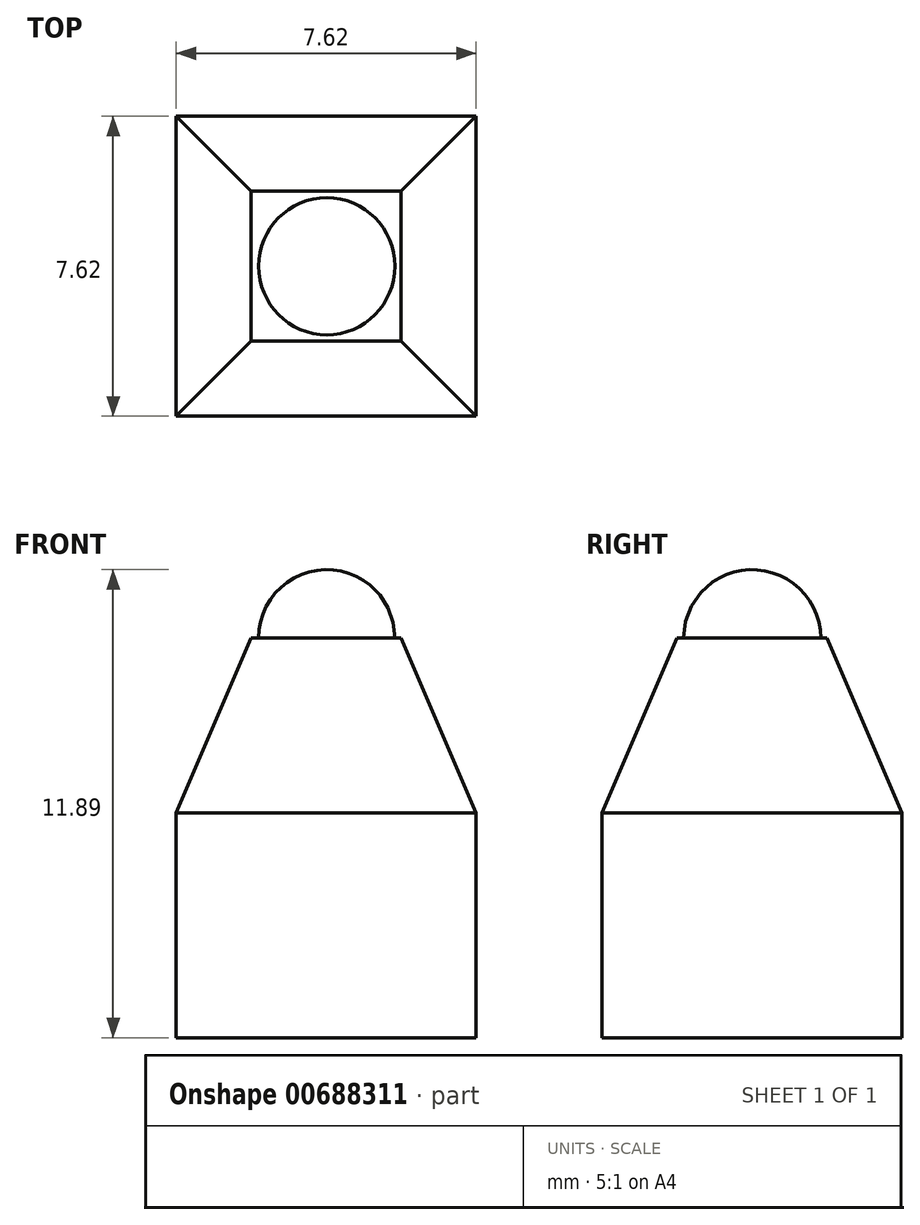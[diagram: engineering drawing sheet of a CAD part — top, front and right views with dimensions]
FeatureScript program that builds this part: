
annotation { "Feature Type Name" : "Feature", "Feature Type Description" : "" }
export const myFeature = defineFeature(function(context is Context, id is Id, definition is map)
    precondition{}
    {
        {
            var Q0;
            Q0=qCreatedBy(makeId("Top.planeOp"),FACE);
            var sketch = newSketch(context, id + "F0", { "sketchPlane" : qUnion([Q0])});
            skLineSegment(sketch, "E0.bottom", {"start": v(0, 0) * mm, "end": v(7.62, 0) * mm});
            skLineSegment(sketch, "E0.top", {"start": v(0, 7.62) * mm, "end": v(7.62, 7.62) * mm});
            skLineSegment(sketch, "E0.left", {"start": v(0, 0) * mm, "end": v(0, 7.62) * mm});
            skLineSegment(sketch, "E0.right", {"start": v(7.62, 0) * mm, "end": v(7.62, 7.62) * mm});
            skSolve(sketch);
        }
        {
            var Q0;
            Q0=makeQuery(id+"F0.imprint","IMPRINT",FACE,{"disambiguationData":[TD([[makeQuery(id+"F0.imprint","IMPRINT",EDGE,{"derivedFrom":sQuery(id+"F0.wireOp",EDGE,"E0.bottom")}),1.0]])]});
            extrude(context, id + "F1", {"entities" : qUnion([Q0]), "depth" : 10.16 * mm, "offsetDistance" : 25.4 * mm});
        }
        {
            var Q0;
            Q0=makeQuery(id+"F1.opExtrude","CAP_EDGE",EDGE,{"disambiguationData":[OSD([sQuery(id+"F0.wireOp",EDGE,"E0.left")])],"isStart":false});
            var Q1;
            Q1=makeQuery(id+"F1.opExtrude","CAP_EDGE",EDGE,{"disambiguationData":[OSD([sQuery(id+"F0.wireOp",EDGE,"E0.right")])],"isStart":false});
            chamfer(context, id + "F2", {"entities" : qUnion([Q0, Q1]), "chamferType" : ChamferType.TWO_OFFSETS, "width1" : 4.44 * mm, "oppositeDirection" : false, "width2" : 1.9 * mm, "tangentPropagation" : true});
        }
        {
            var Q0;
            Q0=makeQuery(id+"F1.opExtrude","CAP_EDGE",EDGE,{"disambiguationData":[OSD([sQuery(id+"F0.wireOp",EDGE,"E0.bottom")])],"isStart":false});
            var Q1;
            Q1=makeQuery(id+"F1.opExtrude","CAP_EDGE",EDGE,{"disambiguationData":[OSD([sQuery(id+"F0.wireOp",EDGE,"E0.top")])],"isStart":false});
            chamfer(context, id + "F3", {"entities" : qUnion([Q0, Q1]), "chamferType" : ChamferType.TWO_OFFSETS, "width1" : 1.9 * mm, "oppositeDirection" : false, "width2" : 4.44 * mm, "tangentPropagation" : true});
        }
        {
            var Q0;
            Q0=makeQuery(id+"F1.opExtrude","CAP_FACE",FACE,{"disambiguationData":[OSD([sQuery(id+"F0.wireOp",EDGE,"E0.bottom"),sQuery(id+"F0.wireOp",EDGE,"E0.top"),sQuery(id+"F0.wireOp",EDGE,"E0.left"),sQuery(id+"F0.wireOp",EDGE,"E0.right")])],"isStart":false});
            var sketch = newSketch(context, id + "F4", { "sketchPlane" : qUnion([Q0])});
            skCircle(sketch, "E1", {"center": v(3.81, 3.8) * mm, "radius": 1.9 * mm});
            skPoint(sketch, "E1.first.point", {"position": v(3.8, 5.71) * mm});
            skPoint(sketch, "E1.second.point", {"position": v(5.71, 3.8) * mm});
            skPoint(sketch, "E1.third.point", {"position": v(3.81, 1.9) * mm});
            skCircle(sketch, "E2", {"center": v(3.81, 3.8) * mm, "radius": 1.75 * mm});
            skLineSegment(sketch, "E3", {"start": v(3.83, 5.56) * mm, "end": v(3.83, 2.06) * mm});
            skSolve(sketch);
        }
        {
            var Q0;
            {var subQ0=sQuery(id+"F4.wireOp",EDGE,"E3");Q0=makeQuery(id+"F4.imprint","IMPRINT",FACE,{"disambiguationData":[TD([[makeQuery(id+"F4.imprint","IMPRINT",EDGE,{"derivedFrom":subQ0}),1.0]])]});}
            var Q1;
            Q1=sQuery(id+"F4.wireOp",EDGE,"E3");
            revolve(context, id + "F5", {"operationType" : NewBodyOperationType.ADD, "surfaceOperationType" : NewSurfaceOperationType.NEW, "entities" : qUnion([Q0]), "axis" : qUnion([Q1]), "revolveType" : RevolveType.FULL});
        }
    });
